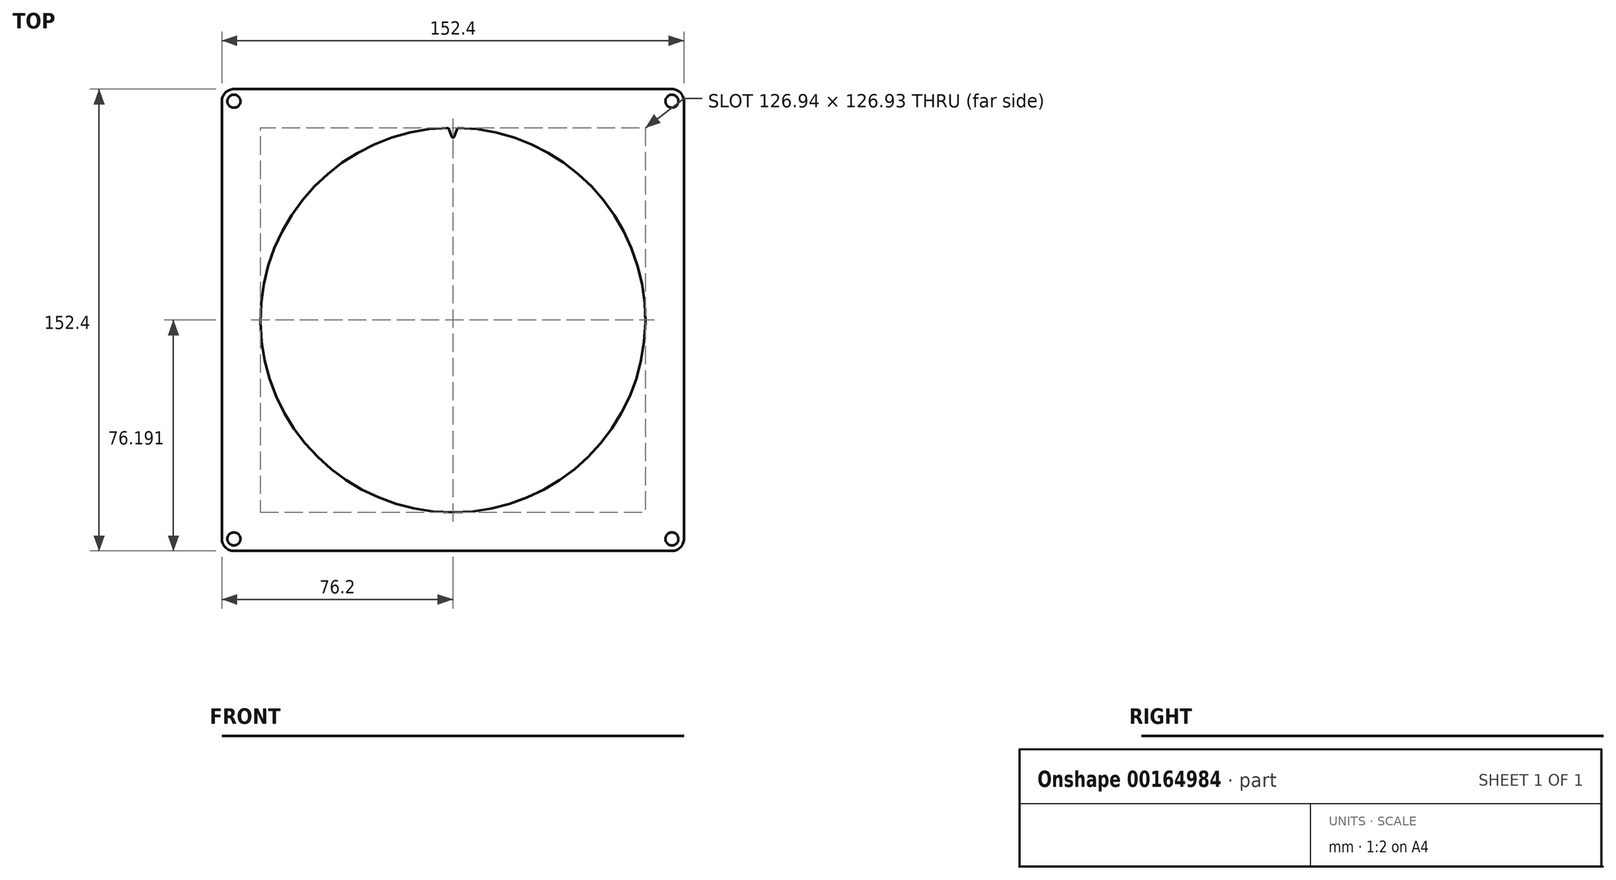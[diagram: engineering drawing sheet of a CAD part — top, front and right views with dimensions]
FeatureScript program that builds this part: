
annotation { "Feature Type Name" : "Feature", "Feature Type Description" : "" }
export const myFeature = defineFeature(function(context is Context, id is Id, definition is map)
    precondition{}
    {
        {
            var Q0;
            Q0=qCreatedBy(makeId("Top.planeOp"),FACE);
            var sketch = newSketch(context, id + "F0", { "sketchPlane" : qUnion([Q0])});
            skCircle(sketch, "E0", {"center": v(0, 0) * mm, "radius": 63.48 * mm});
            skSolve(sketch);
        }
        {
            var Q0;
            Q0 = qSketchRegion(id + "F0", true);
            extrude(context, id + "F1", {"entities" : qUnion([Q0]), "depth" : 3.17 * mm});
        }
        {
            var Q0;
            Q0=makeQuery(id+"F1.opExtrude","CAP_FACE",FACE,{"disambiguationData":[OSD([sQuery(id+"F0.wireOp",EDGE,"E0")])],"isStart":false});
            var sketch = newSketch(context, id + "F2", { "sketchPlane" : qUnion([Q0])});
            skLineSegment(sketch, "E1", {"start": v(0, 0) * mm, "end": v(0, 63.48) * mm, "construction": true});
            skArc(sketch, "E2", {"start": v(1.54, 63.46) * mm, "mid": v(0, 63.48) * mm, "end": v(-1.54, 63.46) * mm});
            skLineSegment(sketch, "E3", {"start": v(-1.54, 63.46) * mm, "end": v(-0.42, 60.52) * mm});
            skLineSegment(sketch, "E4", {"start": v(1.54, 63.46) * mm, "end": v(0.42, 60.52) * mm});
            skArc(sketch, "E5", {"start": v(-0.42, 60.52) * mm, "mid": v(0, 60.23) * mm, "end": v(0.42, 60.52) * mm});
            skLineSegment(sketch, "E6", {"start": v(0, 0) * mm, "end": v(1, 63.47) * mm, "construction": true});
            skPoint(sketch, "E7", {"position": v(0.98, 61.99) * mm});
            skSolve(sketch);
        }
        {
            var Q0;
            Q0 = qSketchRegion(id + "F2", true);
            var Q1;
            Q1=makeQuery(id+"F1.opExtrude","CAP_FACE",FACE,{"disambiguationData":[OSD([sQuery(id+"F0.wireOp",EDGE,"E0")])],"isStart":true});
            extrude(context, id + "F3", {"entities" : qUnion([Q0]), "operationType" : NewBodyOperationType.REMOVE, "endBound" : BoundingType.UP_TO_SURFACE, "oppositeDirection" : true, "endBoundEntityFace" : qUnion([Q1]), "depth" : 25.4 * mm});
        }
        {
            var Q0;
            Q0=makeQuery(id+"F1.opExtrude","CAP_FACE",FACE,{"disambiguationData":[OSD([sQuery(id+"F0.wireOp",EDGE,"E0")])],"isStart":true});
            var sketch = newSketch(context, id + "F4", { "sketchPlane" : qUnion([Q0])});
            skLineSegment(sketch, "E8.bottom", {"start": v(76.2, 76.2) * mm, "end": v(-76.2, 76.2) * mm});
            skLineSegment(sketch, "E8.top", {"start": v(76.2, -76.2) * mm, "end": v(-76.2, -76.2) * mm});
            skLineSegment(sketch, "E8.left", {"start": v(76.2, 76.2) * mm, "end": v(76.2, -76.2) * mm});
            skLineSegment(sketch, "E8.right", {"start": v(-76.2, 76.2) * mm, "end": v(-76.2, -76.2) * mm});
            skPoint(sketch, "E8.middle", {"position": v(0, 0) * mm});
            skLineSegment(sketch, "E9.bottom", {"start": v(72.23, 72.23) * mm, "end": v(-72.23, 72.23) * mm, "construction": true});
            skLineSegment(sketch, "E9.top", {"start": v(72.23, -72.23) * mm, "end": v(-72.23, -72.23) * mm, "construction": true});
            skLineSegment(sketch, "E9.left", {"start": v(72.23, 72.23) * mm, "end": v(72.23, -72.23) * mm, "construction": true});
            skLineSegment(sketch, "E9.right", {"start": v(-72.23, 72.23) * mm, "end": v(-72.23, -72.23) * mm, "construction": true});
            skLineSegment(sketch, "E10", {"start": v(0, 72.23) * mm, "end": v(0, 76.2) * mm, "construction": true});
            skCircle(sketch, "E11", {"center": v(72.23, 72.23) * mm, "radius": 2.15 * mm});
            skCircle(sketch, "E12", {"center": v(-72.23, 72.23) * mm, "radius": 2.15 * mm});
            skCircle(sketch, "E13", {"center": v(-72.23, -72.23) * mm, "radius": 2.15 * mm});
            skCircle(sketch, "E14", {"center": v(72.23, -72.23) * mm, "radius": 2.15 * mm});
            skSolve(sketch);
        }
        {
            var Q0;
            Q0=makeQuery(id+"F4.imprint","IMPRINT",FACE,{"disambiguationData":[TD([[makeQuery(id+"F4.imprint","IMPRINT",EDGE,{"derivedFrom":sQuery(id+"F4.wireOp",EDGE,"E8.bottom")}),1.0]])]});
            extrude(context, id + "F5", {"entities" : qUnion([Q0]), "depth" : 1 / 203.2 * mm});
        }
        {
            var Q0;
            Q0=makeQuery(id+"F1.opExtrude","CAP_FACE",FACE,{"disambiguationData":[OSD([sQuery(id+"F0.wireOp",EDGE,"E0")])],"isStart":false});
            var Q1;
            Q1=makeQuery(id+"F5.opExtrude","CAP_FACE",FACE,{"disambiguationData":[OSD([sQuery(id+"F0.wireOp",EDGE,"E0"),sQuery(id+"F2.wireOp",EDGE,"E3"),sQuery(id+"F2.wireOp",EDGE,"E4"),sQuery(id+"F2.wireOp",EDGE,"E5"),sQuery(id+"F4.wireOp",EDGE,"E8.bottom"),sQuery(id+"F4.wireOp",EDGE,"E8.top"),sQuery(id+"F4.wireOp",EDGE,"E8.left"),sQuery(id+"F4.wireOp",EDGE,"E8.right"),sQuery(id+"F4.wireOp",EDGE,"E11"),sQuery(id+"F4.wireOp",EDGE,"E12"),sQuery(id+"F4.wireOp",EDGE,"E13"),sQuery(id+"F4.wireOp",EDGE,"E14")])],"isStart":true});
            extrude(context, id + "F6", {"entities" : qUnion([Q0]), "operationType" : NewBodyOperationType.REMOVE, "endBound" : BoundingType.UP_TO_SURFACE, "oppositeDirection" : true, "endBoundEntityFace" : qUnion([Q1]), "depth" : 25.4 * mm});
        }
        {
            var Q0;
            Q0=makeQuery(id+"F5.opExtrude","SWEPT_EDGE",EDGE,{"disambiguationData":[OSD([sQuery(id+"F4.wireOp",EDGE,"E8.bottom"),sQuery(id+"F4.wireOp",EDGE,"E8.left")])]});
            var Q1;
            Q1=makeQuery(id+"F5.opExtrude","SWEPT_EDGE",EDGE,{"disambiguationData":[OSD([sQuery(id+"F4.wireOp",EDGE,"E8.bottom"),sQuery(id+"F4.wireOp",EDGE,"E8.right")])]});
            var Q2;
            Q2=makeQuery(id+"F5.opExtrude","SWEPT_EDGE",EDGE,{"disambiguationData":[OSD([sQuery(id+"F4.wireOp",EDGE,"E8.top"),sQuery(id+"F4.wireOp",EDGE,"E8.right")])]});
            var Q3;
            Q3=makeQuery(id+"F5.opExtrude","SWEPT_EDGE",EDGE,{"disambiguationData":[OSD([sQuery(id+"F4.wireOp",EDGE,"E8.top"),sQuery(id+"F4.wireOp",EDGE,"E8.left")])]});
            fillet(context, id + "F7", {"entities" : qUnion([Q0, Q1, Q2, Q3]), "radius" : 3.97 * mm, "tangentPropagation" : true, "allowEdgeOverflow" : false});
        }
    });
